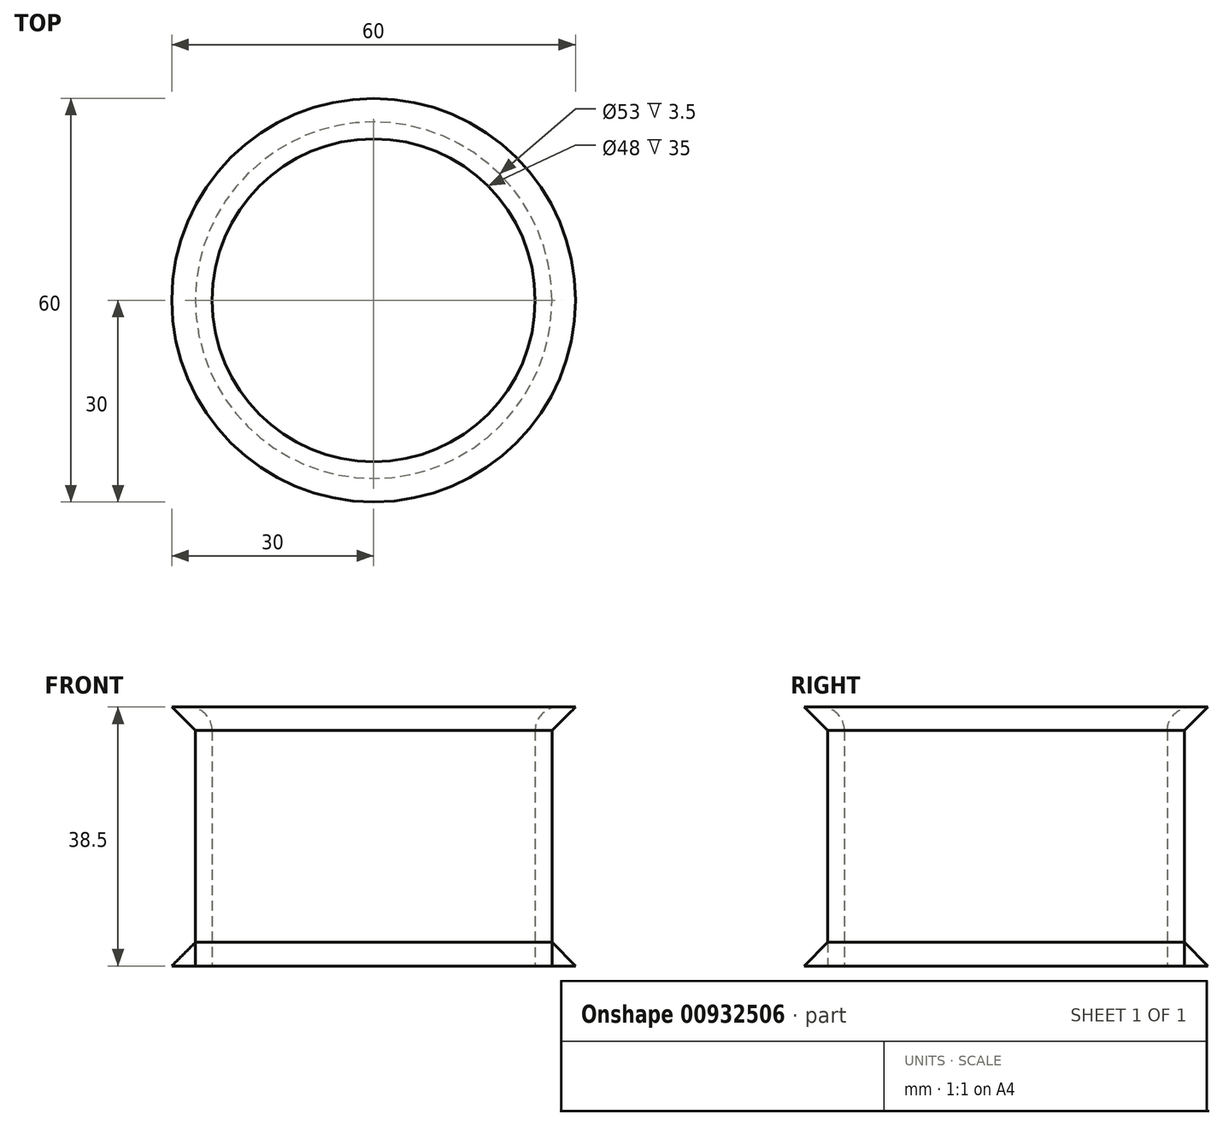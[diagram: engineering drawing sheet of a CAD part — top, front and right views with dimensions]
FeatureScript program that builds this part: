
annotation { "Feature Type Name" : "Feature", "Feature Type Description" : "" }
export const myFeature = defineFeature(function(context is Context, id is Id, definition is map)
    precondition{}
    {
        {
            assignVariable(context, id + "F0", {"name" : "Overhang", "anyValue" : 3.5 * mm});
        }
        {
            assignVariable(context, id + "F1", {"name" : "Height", "anyValue" : 38.5 * mm});
        }
        {
            var Q0;
            Q0=qCreatedBy(makeId("Top.planeOp"),FACE);
            var sketch = newSketch(context, id + "F2", { "sketchPlane" : qUnion([Q0])});
            skCircle(sketch, "E0", {"center": v(0, 0) * mm, "radius": 26.5 * mm});
            skCircle(sketch, "E1", {"center": v(0, 0) * mm, "radius": 24 * mm});
            skSolve(sketch);
        }
        {
            var Q0;
            Q0=makeQuery(id+"F2.imprint","IMPRINT",FACE,{"disambiguationData":[TD([[makeQuery(id+"F2.imprint","IMPRINT",EDGE,{"derivedFrom":sQuery(id+"F2.wireOp",EDGE,"E0")}),1.0]])]});
            extrude(context, id + "F3", {"entities" : qUnion([Q0]), "depth" : getVariable(context, 'Height'), "offsetDistance" : 25.4 * mm});
        }
        {
            var Q0;
            Q0=qCreatedBy(makeId("Right.planeOp"),FACE);
            var sketch = newSketch(context, id + "F4", { "sketchPlane" : qUnion([Q0])});
            skLineSegment(sketch, "E2", {"start": v(-26.5, 35) * mm, "end": v(-26.5, 38.5) * mm});
            skLineSegment(sketch, "E3", {"start": v(-26.5, 38.5) * mm, "end": v(-30, 38.5) * mm});
            skLineSegment(sketch, "E4", {"start": v(-30, 38.5) * mm, "end": v(-26.5, 35) * mm});
            skLineSegment(sketch, "E5.0", {"start": v(-26.5, 38.5) * mm, "end": v(26.5, 38.5) * mm, "construction": true});
            skLineSegment(sketch, "E6.0", {"start": v(-26.5, 0) * mm, "end": v(26.5, 0) * mm, "construction": true});
            skLineSegment(sketch, "E7", {"start": v(-26.5, 0) * mm, "end": v(-26.5, 38.5) * mm, "construction": true});
            skLineSegment(sketch, "E8", {"start": v(26.5, 38.5) * mm, "end": v(26.5, 0) * mm, "construction": true});
            skLineSegment(sketch, "E9", {"start": v(26.5, 19.25) * mm, "end": v(-26.5, 19.25) * mm, "construction": true});
            skLineSegment(sketch, "E10.MirrorCS", {"start": v(-26.5, 0) * mm, "end": v(-30, 0) * mm});
            skLineSegment(sketch, "E11.MirrorCS", {"start": v(-26.5, 3.5) * mm, "end": v(-26.5, 0) * mm});
            skLineSegment(sketch, "E12.MirrorCS", {"start": v(-26.5, 38.5) * mm, "end": v(-26.5, 0) * mm, "construction": true});
            skLineSegment(sketch, "E13.MirrorCS", {"start": v(-30, 0) * mm, "end": v(-26.5, 3.5) * mm});
            skLineSegment(sketch, "E14", {"start": v(0, 38.5) * mm, "end": v(0, 0) * mm, "construction": true});
            skSolve(sketch);
        }
        {
            var Q0;
            Q0=makeQuery(id+"F4.imprint","IMPRINT",FACE,{"disambiguationData":[TD([[makeQuery(id+"F4.imprint","IMPRINT",EDGE,{"derivedFrom":sQuery(id+"F4.wireOp",EDGE,"E2")}),1.0]])]});
            var Q1;
            Q1=sQuery(id+"F4.wireOp",EDGE,"E14");
            revolve(context, id + "F5", {"operationType" : NewBodyOperationType.ADD, "surfaceOperationType" : NewSurfaceOperationType.NEW, "entities" : qUnion([Q0]), "axis" : qUnion([Q1]), "revolveType" : RevolveType.FULL});
        }
        {
            var Q0;
            Q0=makeQuery(id+"F4.imprint","IMPRINT",FACE,{"disambiguationData":[TD([[makeQuery(id+"F4.imprint","IMPRINT",EDGE,{"derivedFrom":sQuery(id+"F4.wireOp",EDGE,"E10.MirrorCS")}),-1.0]])]});
            var Q1;
            Q1=makeQuery(id+"F3.opExtrude","SWEPT_FACE",FACE,{"disambiguationData":[OSD([sQuery(id+"F2.wireOp",EDGE,"E1")])]});
            revolve(context, id + "F6", {"surfaceOperationType" : NewSurfaceOperationType.NEW, "entities" : qUnion([Q0]), "axis" : qUnion([Q1]), "revolveType" : RevolveType.FULL});
        }
        {
            var Q0;
            Q0=makeQuery(id+"F3.opExtrude","CAP_EDGE",EDGE,{"disambiguationData":[OSD([sQuery(id+"F2.wireOp",EDGE,"E1")])],"isStart":false});
            fillet(context, id + "F7", {"entities" : qUnion([Q0]), "radius" : getVariable(context, 'Overhang'), "tangentPropagation" : true, "allowEdgeOverflow" : false});
        }
    });
